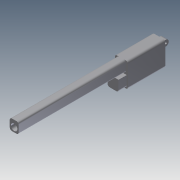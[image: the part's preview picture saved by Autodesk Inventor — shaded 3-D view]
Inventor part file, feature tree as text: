
AUTODESK INVENTOR PART (.ipt)
format: ipt  version: 2011 (Build 150239000, 239)  size: 232,960 bytes
history: native  units: in
note: dims shown in document units (in); Inventor stores cm internally (conversion verified against a paired STEP export)
features: extrude x14, sketch x14, fillet x1
ambient origin geometry x8: Origin, YZ Plane, XZ Plane, XY Plane, X Axis, Y Axis, Z Axis, Center Point
bodies: Solid1 (feature_tree)
feature tree (29):
  extrude  "Extrusion1"  Depth=2.91in
  extrude  "Extrusion2"  Depth=1.56in
  extrude  "Extrusion3"  Depth=0.25in
  extrude  "Extrusion4"  Depth=6.4in TaperAngle=0.0deg
  extrude  "Extrusion5"  Depth=8.0in TaperAngle=0.0deg
  extrude  "Extrusion6"  Depth=1.31in
  extrude  "Extrusion7"  Depth=1.0in TaperAngle=0.0deg
  extrude  "Extrusion8"  Depth=0.7in
  extrude  "Extrusion9"  Depth=0.25in
  extrude  "Extrusion10"  Depth=0.7in TaperAngle=0.0deg
  fillet  "Fillet1"  Radius=1.5in
  extrude  "Extrusion11"  Depth=0.78in
  extrude  "Extrusion12"  Depth=9.0in TaperAngle=0.0deg
  extrude  "Extrusion13"  Depth=8.0in TaperAngle=0.0deg
  extrude  "Extrusion14"  [1 undecoded]
  sketch  "Sketch1"  dims[d0=1.56in d1=2.91in]
  sketch  "Sketch2"  dims[d2=3.0in d3=0.0in d4=1.56in]
  sketch  "Sketch3"  dims[d5=0.25in d6=0.25in]
  sketch  "Sketch4"  dims[d7=1.06in d8=6.4in d9=0.0in]
  sketch  "Sketch5"  dims[d10=0.78in d11=8.0in d12=0.0in]
  sketch  "Sketch6"  dims[d13=1.0in d14=0.0in d15=1.31in]
  sketch  "Sketch7"  dims[d16=3.5in d17=0.0in d18=1.0in d19=0.0in]
  sketch  "Sketch8"  dims[d20=45.0deg d21=0.7in]
  sketch  "Sketch9"  dims[d22=0.5in d23=0.0in d24=0.25in]
  sketch  "Sketch10"  dims[d25=1.0in d26=0.0in d27=0.7in d28=0.0in d29=1.5in d30=0.0in]
  sketch  "Sketch11"  dims[d31=0.25in d32=0.78in]
  sketch  "Sketch12"  dims[d33=4.0in d34=0.0in d35=9.0in d36=0.0in]
  sketch  "Sketch13"  dims[d37=4.0in d38=0.0in d39=8.0in d40=0.0in]
  sketch  "Sketch14"
note: 1 required parameter value undecoded (feature->parameter linkage not recoverable at this tier; creation-order binding heuristic only, values carry confidence <= 0.55)
